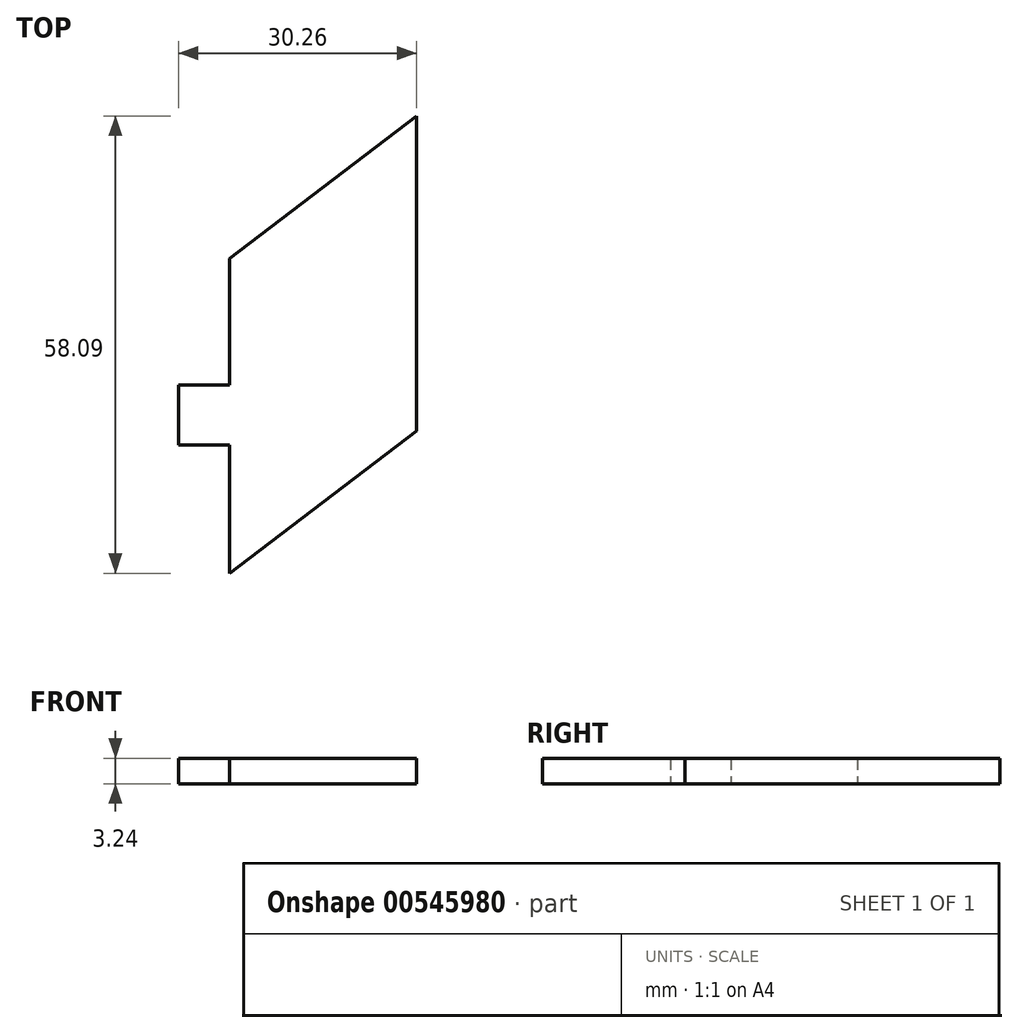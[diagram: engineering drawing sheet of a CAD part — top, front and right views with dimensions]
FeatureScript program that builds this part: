
annotation { "Feature Type Name" : "Feature", "Feature Type Description" : "" }
export const myFeature = defineFeature(function(context is Context, id is Id, definition is map)
    precondition{}
    {
        {
            var Q0;
            Q0=qCreatedBy(makeId("Top.planeOp"),FACE);
            var sketch = newSketch(context, id + "F0", { "sketchPlane" : qUnion([Q0])});
            skLineSegment(sketch, "E0", {"start": v(0, 29.82) * mm, "end": v(0, -22.15) * mm});
            skLineSegment(sketch, "E1", {"start": v(8.33, 29.57) * mm, "end": v(8.33, -10.43) * mm});
            skLineSegment(sketch, "E2", {"start": v(8.33, 29.57) * mm, "end": v(32.1, 47.66) * mm});
            skLineSegment(sketch, "E3", {"start": v(32.1, 47.66) * mm, "end": v(32.1, 7.66) * mm});
            skLineSegment(sketch, "E4", {"start": v(8.33, -10.43) * mm, "end": v(32.1, 7.66) * mm});
            skLineSegment(sketch, "E5", {"start": v(8.33, 9.57) * mm, "end": v(8.33, 13.5) * mm});
            skLineSegment(sketch, "E6", {"start": v(8.33, 13.5) * mm, "end": v(1.84, 13.5) * mm});
            skLineSegment(sketch, "E7", {"start": v(1.84, 13.5) * mm, "end": v(1.84, 5.85) * mm});
            skLineSegment(sketch, "E8", {"start": v(1.84, 5.85) * mm, "end": v(8.33, 5.85) * mm});
            skLineSegment(sketch, "E9", {"start": v(8.33, 5.85) * mm, "end": v(8.33, 9.57) * mm});
            skSolve(sketch);
        }
        {
            var Q0;
            Q0 = qSketchRegion(id + "F0", true);
            extrude(context, id + "F1", {"entities" : qUnion([Q0]), "depth" : 3.24 * mm, "offsetDistance" : 25 * mm});
        }
    });
